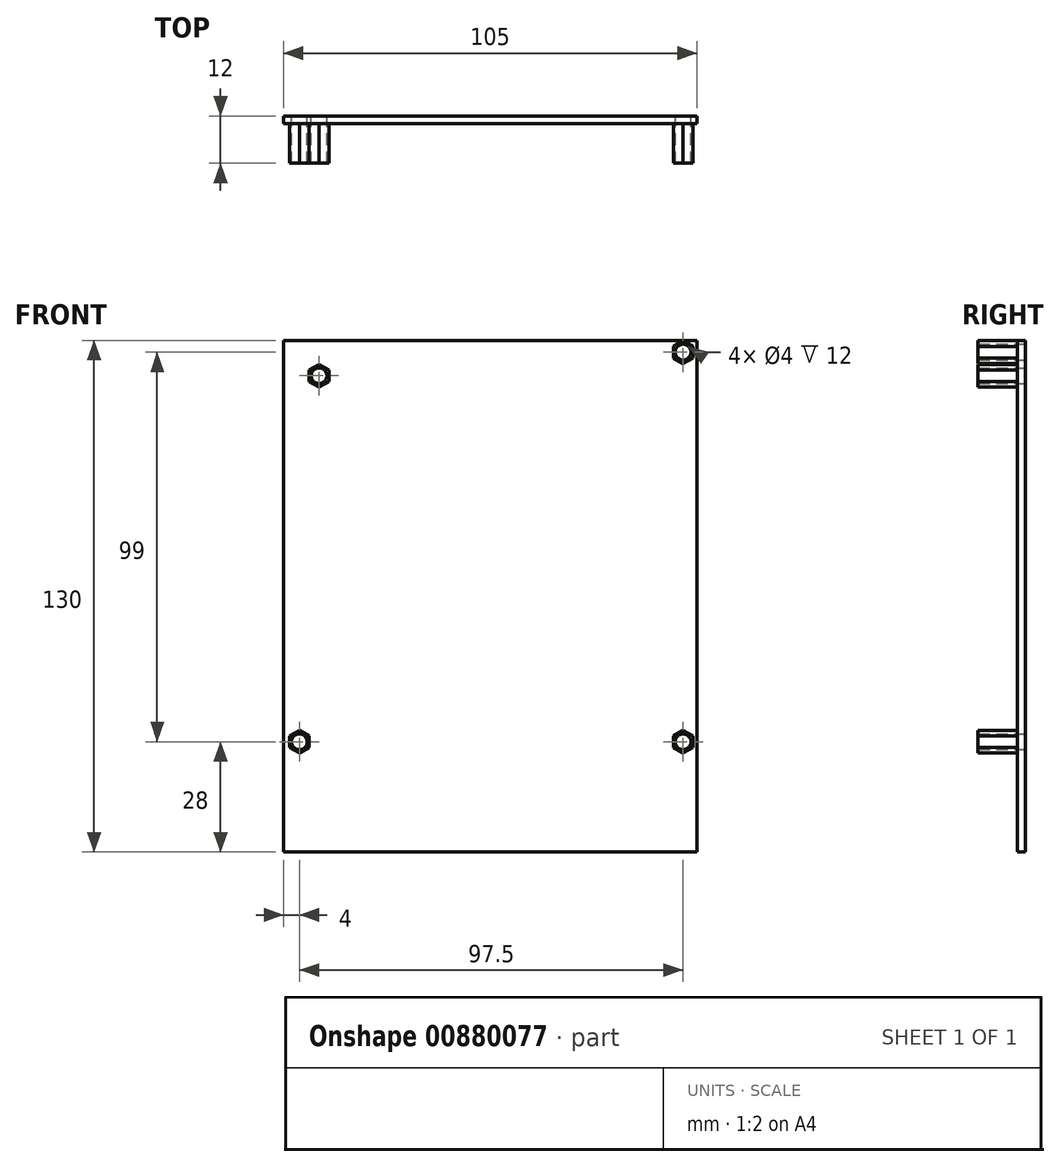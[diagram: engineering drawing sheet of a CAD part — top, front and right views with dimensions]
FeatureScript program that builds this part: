
annotation { "Feature Type Name" : "Feature", "Feature Type Description" : "" }
export const myFeature = defineFeature(function(context is Context, id is Id, definition is map)
    precondition{}
    {
        {
            var Q0;
            Q0=qCreatedBy(makeId("Front.planeOp"),FACE);
            var sketch = newSketch(context, id + "F0", { "sketchPlane" : qUnion([Q0])});
            skLineSegment(sketch, "E0.bottom", {"start": v(52.5, 65) * mm, "end": v(-52.5, 65) * mm});
            skLineSegment(sketch, "E0.top", {"start": v(52.5, -65) * mm, "end": v(-52.5, -65) * mm});
            skLineSegment(sketch, "E0.left", {"start": v(52.5, 65) * mm, "end": v(52.5, -65) * mm});
            skLineSegment(sketch, "E0.right", {"start": v(-52.5, 65) * mm, "end": v(-52.5, -65) * mm});
            skPoint(sketch, "E0.middle", {"position": v(0, 0) * mm});
            skCircle(sketch, "E1", {"center": v(49, 62) * mm, "radius": 2 * mm});
            skCircle(sketch, "E2", {"center": v(49, -37) * mm, "radius": 2 * mm});
            skCircle(sketch, "E3", {"center": v(-48.5, -37) * mm, "radius": 2 * mm});
            skCircle(sketch, "E4", {"center": v(-43.5, 56) * mm, "radius": 2 * mm});
            skSolve(sketch);
        }
        {
            var Q0;
            Q0=makeQuery(id+"F0.imprint","IMPRINT",FACE,{"disambiguationData":[TD([[makeQuery(id+"F0.imprint","IMPRINT",EDGE,{"derivedFrom":sQuery(id+"F0.wireOp",EDGE,"E0.bottom")}),1.0]])]});
            extrude(context, id + "F1", {"entities" : qUnion([Q0]), "depth" : 2 * mm});
        }
        {
            var Q0;
            Q0=makeQuery(id+"F1.opExtrude","CAP_FACE",FACE,{"disambiguationData":[OSD([sQuery(id+"F0.wireOp",EDGE,"E0.bottom"),sQuery(id+"F0.wireOp",EDGE,"E0.top"),sQuery(id+"F0.wireOp",EDGE,"E0.left"),sQuery(id+"F0.wireOp",EDGE,"E0.right"),sQuery(id+"F0.wireOp",EDGE,"E1"),sQuery(id+"F0.wireOp",EDGE,"E2"),sQuery(id+"F0.wireOp",EDGE,"E3"),sQuery(id+"F0.wireOp",EDGE,"E4")])],"isStart":false});
            var sketch = newSketch(context, id + "F2", { "sketchPlane" : qUnion([Q0])});
            skCircle(sketch, "E5.cCircle", {"center": v(-43.5, 56) * mm, "radius": 2.5 * mm, "construction": true});
            skLineSegment(sketch, "E5.0", {"start": v(-41, 57.44) * mm, "end": v(-41, 54.56) * mm});
            skLineSegment(sketch, "E5.1", {"start": v(-41, 54.56) * mm, "end": v(-43.5, 53.11) * mm});
            skLineSegment(sketch, "E5.2", {"start": v(-43.5, 53.11) * mm, "end": v(-46, 54.56) * mm});
            skLineSegment(sketch, "E5.3", {"start": v(-46, 54.56) * mm, "end": v(-46, 57.44) * mm});
            skLineSegment(sketch, "E5.4", {"start": v(-46, 57.44) * mm, "end": v(-43.5, 58.89) * mm});
            skLineSegment(sketch, "E5.5", {"start": v(-43.5, 58.89) * mm, "end": v(-41, 57.44) * mm});
            skPoint(sketch, "E5.0.midPoint", {"position": v(-41, 56) * mm});
            skCircle(sketch, "E6.cCircle", {"center": v(49, 62) * mm, "radius": 2.5 * mm, "construction": true});
            skLineSegment(sketch, "E6.0", {"start": v(51.5, 63.44) * mm, "end": v(51.5, 60.56) * mm});
            skLineSegment(sketch, "E6.1", {"start": v(51.5, 60.56) * mm, "end": v(49, 59.11) * mm});
            skLineSegment(sketch, "E6.2", {"start": v(49, 59.11) * mm, "end": v(46.5, 60.56) * mm});
            skLineSegment(sketch, "E6.3", {"start": v(46.5, 60.56) * mm, "end": v(46.5, 63.44) * mm});
            skLineSegment(sketch, "E6.4", {"start": v(46.5, 63.44) * mm, "end": v(49, 64.89) * mm});
            skLineSegment(sketch, "E6.5", {"start": v(49, 64.89) * mm, "end": v(51.5, 63.44) * mm});
            skPoint(sketch, "E6.0.midPoint", {"position": v(51.5, 62) * mm});
            skCircle(sketch, "E7.cCircle", {"center": v(-48.5, -37) * mm, "radius": 2.5 * mm, "construction": true});
            skLineSegment(sketch, "E7.0", {"start": v(-46, -35.56) * mm, "end": v(-46, -38.44) * mm});
            skLineSegment(sketch, "E7.1", {"start": v(-46, -38.44) * mm, "end": v(-48.5, -39.89) * mm});
            skLineSegment(sketch, "E7.2", {"start": v(-48.5, -39.89) * mm, "end": v(-51, -38.44) * mm});
            skLineSegment(sketch, "E7.3", {"start": v(-51, -38.44) * mm, "end": v(-51, -35.56) * mm});
            skLineSegment(sketch, "E7.4", {"start": v(-51, -35.56) * mm, "end": v(-48.5, -34.11) * mm});
            skLineSegment(sketch, "E7.5", {"start": v(-48.5, -34.11) * mm, "end": v(-46, -35.56) * mm});
            skPoint(sketch, "E7.0.midPoint", {"position": v(-46, -37) * mm});
            skCircle(sketch, "E8.cCircle", {"center": v(49, -37) * mm, "radius": 2.5 * mm, "construction": true});
            skLineSegment(sketch, "E8.0", {"start": v(46.5, -38.44) * mm, "end": v(46.5, -35.56) * mm});
            skLineSegment(sketch, "E8.1", {"start": v(46.5, -35.56) * mm, "end": v(49, -34.11) * mm});
            skLineSegment(sketch, "E8.2", {"start": v(49, -34.11) * mm, "end": v(51.5, -35.56) * mm});
            skLineSegment(sketch, "E8.3", {"start": v(51.5, -35.56) * mm, "end": v(51.5, -38.44) * mm});
            skLineSegment(sketch, "E8.4", {"start": v(51.5, -38.44) * mm, "end": v(49, -39.89) * mm});
            skLineSegment(sketch, "E8.5", {"start": v(49, -39.89) * mm, "end": v(46.5, -38.44) * mm});
            skPoint(sketch, "E8.0.midPoint", {"position": v(46.5, -37) * mm});
            skSolve(sketch);
        }
        {
            var Q0;
            Q0=makeQuery(id+"F2.imprint","IMPRINT",FACE,{"disambiguationData":[TD([[makeQuery(id+"F2.imprint","IMPRINT",EDGE,{"derivedFrom":sQuery(id+"F2.wireOp",EDGE,"E5.0")}),-1.0]])]});
            var Q1;
            Q1=makeQuery(id+"F2.imprint","IMPRINT",FACE,{"disambiguationData":[TD([[makeQuery(id+"F2.imprint","IMPRINT",EDGE,{"derivedFrom":sQuery(id+"F2.wireOp",EDGE,"E6.0")}),-1.0]])]});
            var Q2;
            Q2=makeQuery(id+"F2.imprint","IMPRINT",FACE,{"disambiguationData":[TD([[makeQuery(id+"F2.imprint","IMPRINT",EDGE,{"derivedFrom":sQuery(id+"F2.wireOp",EDGE,"E7.0")}),-1.0]])]});
            var Q3;
            Q3=makeQuery(id+"F2.imprint","IMPRINT",FACE,{"disambiguationData":[TD([[makeQuery(id+"F2.imprint","IMPRINT",EDGE,{"derivedFrom":sQuery(id+"F2.wireOp",EDGE,"E8.0")}),-1.0]])]});
            extrude(context, id + "F3", {"entities" : qUnion([Q0, Q1, Q2, Q3]), "operationType" : NewBodyOperationType.ADD, "depth" : 10 * mm});
        }
    });
